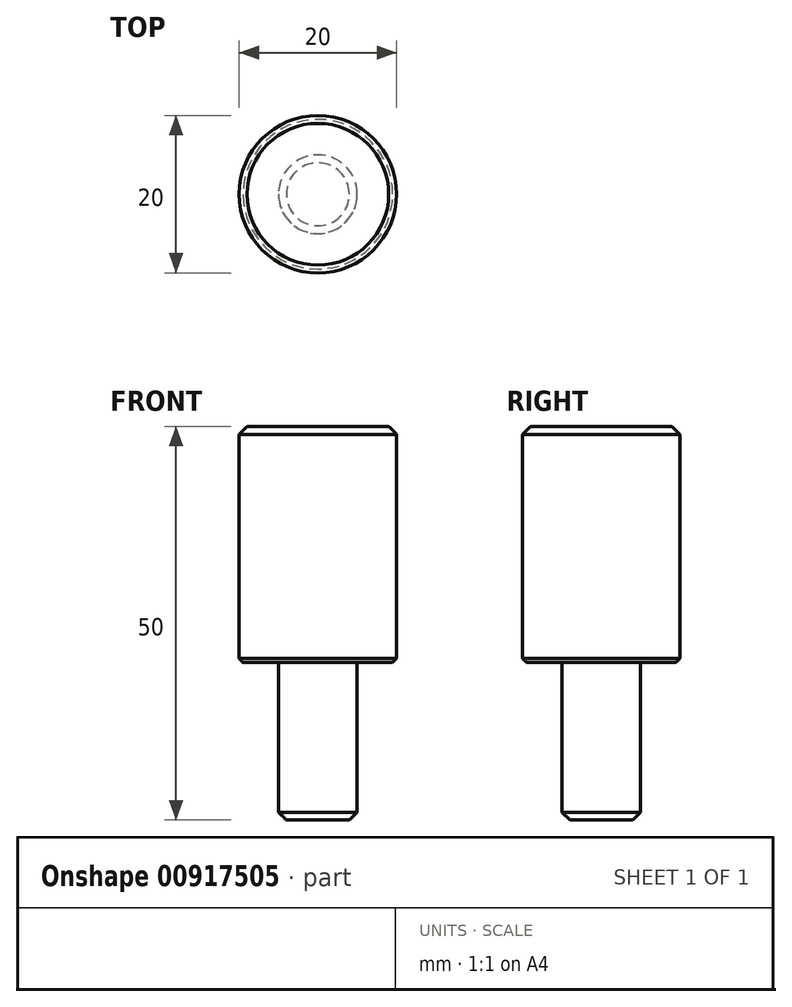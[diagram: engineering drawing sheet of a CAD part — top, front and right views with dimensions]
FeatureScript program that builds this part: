
annotation { "Feature Type Name" : "Feature", "Feature Type Description" : "" }
export const myFeature = defineFeature(function(context is Context, id is Id, definition is map)
    precondition{}
    {
        {
            var Q0;
            Q0=qCreatedBy(makeId("Front.planeOp"),FACE);
            var sketch = newSketch(context, id + "F0", { "sketchPlane" : qUnion([Q0])});
            skLineSegment(sketch, "E0", {"start": v(0, 30) * mm, "end": v(10, 30) * mm});
            skLineSegment(sketch, "E1", {"start": v(10, 30) * mm, "end": v(10, 0) * mm});
            skLineSegment(sketch, "E2", {"start": v(10, 0) * mm, "end": v(5, 0) * mm});
            skLineSegment(sketch, "E3", {"start": v(5, 0) * mm, "end": v(5, -20) * mm});
            skLineSegment(sketch, "E4", {"start": v(5, -20) * mm, "end": v(0, -20) * mm});
            skLineSegment(sketch, "E5", {"start": v(0, 30) * mm, "end": v(0, -20) * mm, "construction": true});
            skLineSegment(sketch, "E6", {"start": v(0, 30) * mm, "end": v(0, -20) * mm});
            skSolve(sketch);
        }
        {
            var Q0;
            Q0 = qSketchRegion(id + "F0", true);
            var Q1;
            Q1=sQuery(id+"F0.wireOp",EDGE,"E5");
            revolve(context, id + "F1", {"surfaceOperationType" : NewSurfaceOperationType.NEW, "entities" : qUnion([Q0]), "axis" : qUnion([Q1]), "revolveType" : RevolveType.FULL});
        }
        {
            var Q0;
            Q0=makeQuery(id+"F1.opRevolve","SWEPT_EDGE",EDGE,{"disambiguationData":[OSD([sQuery(id+"F0.wireOp",EDGE,"E0"),sQuery(id+"F0.wireOp",EDGE,"E1")])]});
            var Q1;
            Q1=makeQuery(id+"F1.opRevolve","SWEPT_EDGE",EDGE,{"disambiguationData":[OSD([sQuery(id+"F0.wireOp",EDGE,"E3"),sQuery(id+"F0.wireOp",EDGE,"E4")])]});
            chamfer(context, id + "F2", {"entities" : qUnion([Q0, Q1]), "width" : 1 * mm, "tangentPropagation" : true});
        }
        {
            var Q0;
            Q0=makeQuery(id+"F1.opRevolve","SWEPT_EDGE",EDGE,{"disambiguationData":[OSD([sQuery(id+"F0.wireOp",EDGE,"E1"),sQuery(id+"F0.wireOp",EDGE,"E2")])]});
            chamfer(context, id + "F3", {"entities" : qUnion([Q0]), "width" : 0.5 * mm, "tangentPropagation" : true});
        }
    });
